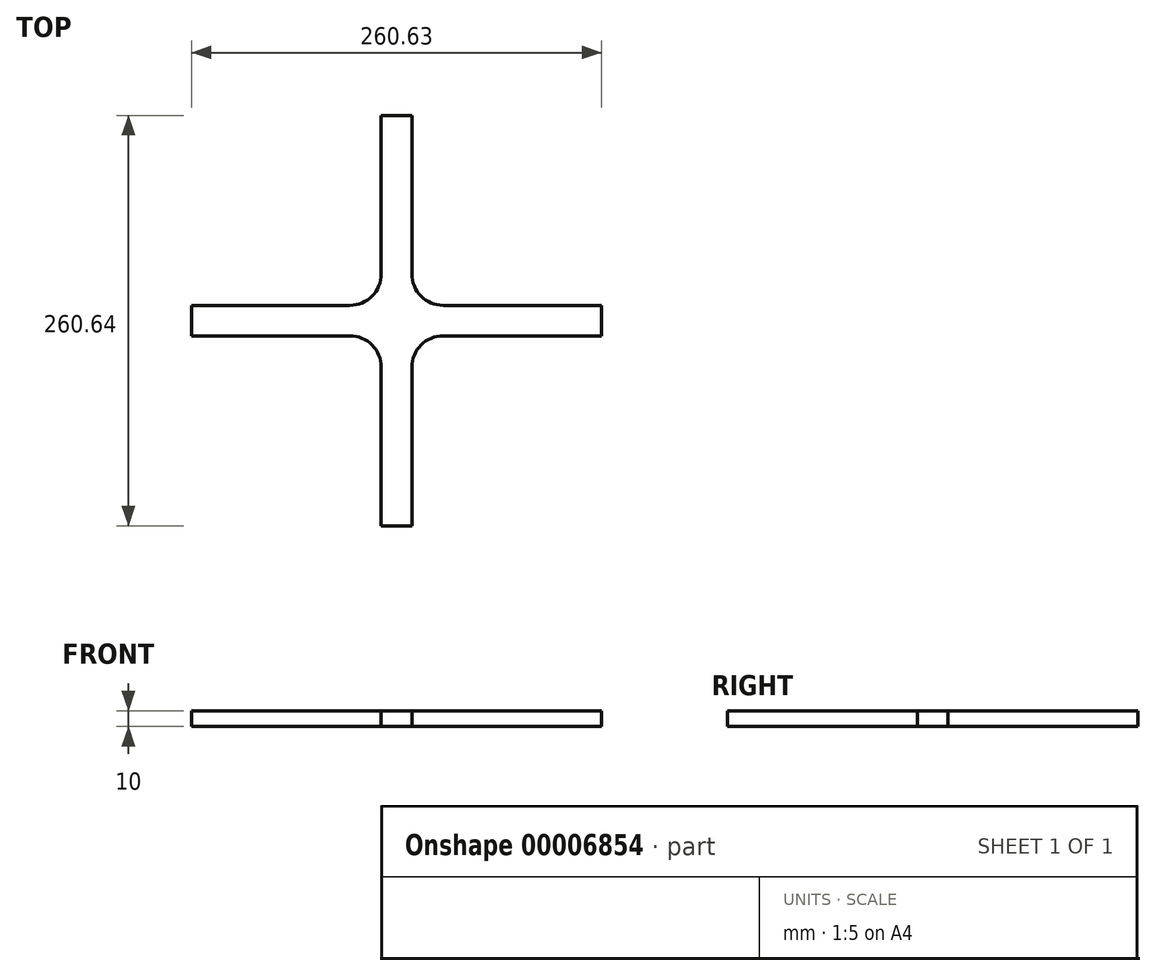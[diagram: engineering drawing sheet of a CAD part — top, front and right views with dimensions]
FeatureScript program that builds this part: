
annotation { "Feature Type Name" : "Feature", "Feature Type Description" : "" }
export const myFeature = defineFeature(function(context is Context, id is Id, definition is map)
    precondition{}
    {
        {
            var Q0;
            Q0=qCreatedBy(makeId("Top.planeOp"),FACE);
            var sketch = newSketch(context, id + "F0", { "sketchPlane" : qUnion([Q0])});
            skLineSegment(sketch, "E0.bottom", {"start": v(21.97, 150.47) * mm, "end": v(41.97, 150.47) * mm});
            skLineSegment(sketch, "E0.top", {"start": v(21.97, -110.77) * mm, "end": v(41.97, -110.77) * mm});
            skLineSegment(sketch, "E0.left", {"start": v(21.97, 150.47) * mm, "end": v(21.97, -110.77) * mm});
            skLineSegment(sketch, "E0.right", {"start": v(41.97, 150.47) * mm, "end": v(41.97, -110.77) * mm});
            skLineSegment(sketch, "E1.bottom", {"start": v(-98.64, 29.85) * mm, "end": v(162.6, 29.85) * mm});
            skLineSegment(sketch, "E1.top", {"start": v(-98.64, 9.85) * mm, "end": v(162.6, 9.85) * mm});
            skLineSegment(sketch, "E1.left", {"start": v(-98.64, 29.85) * mm, "end": v(-98.64, 9.85) * mm});
            skLineSegment(sketch, "E1.right", {"start": v(162.6, 29.85) * mm, "end": v(162.6, 9.85) * mm});
            skPoint(sketch, "E2", {"position": v(31.97, 150.47) * mm});
            skPoint(sketch, "E3", {"position": v(162.6, 19.85) * mm});
            skPoint(sketch, "E4", {"position": v(41.97, 19.85) * mm});
            skPoint(sketch, "E5", {"position": v(31.97, 29.85) * mm});
            skCircle(sketch, "E6", {"center": v(31.97, 19.85) * mm, "radius": 131 * mm});
            skLineSegment(sketch, "E7.0", {"start": v(-98.64, 10.15) * mm, "end": v(162.6, 10.15) * mm});
            skLineSegment(sketch, "E8.0", {"start": v(-98.64, 29.55) * mm, "end": v(162.6, 29.55) * mm});
            skLineSegment(sketch, "E9.0", {"start": v(22.27, 150.47) * mm, "end": v(22.27, -110.77) * mm});
            skLineSegment(sketch, "E10.0", {"start": v(41.67, 150.47) * mm, "end": v(41.67, -110.77) * mm});
            skLineSegment(sketch, "E11.0", {"start": v(-98.34, 29.85) * mm, "end": v(-98.34, 9.85) * mm});
            skLineSegment(sketch, "E12.0", {"start": v(21.97, 150.17) * mm, "end": v(41.97, 150.17) * mm});
            skLineSegment(sketch, "E13.0", {"start": v(162.3, 29.85) * mm, "end": v(162.3, 9.85) * mm});
            skLineSegment(sketch, "E14.0", {"start": v(21.97, -110.47) * mm, "end": v(41.97, -110.47) * mm});
            skSolve(sketch);
        }
        {
            var Q0;
            {var subQ0=sQuery(id+"F0.wireOp",EDGE,"E8.0");var subQ1=sQuery(id+"F0.wireOp",EDGE,"E0.left");var subQ2=makeQuery(id+"F0.imprint","INTERSECT",VERTEX,{"derivedFrom":[subQ1,subQ0]});Q0=makeQuery(id+"F0.imprint","IMPRINT",FACE,{"disambiguationData":[TD([[makeQuery(id+"F0.imprint","IMPRINT",EDGE,{"disambiguationData":[TD([[subQ2,-1.0]])],"derivedFrom":subQ1}),-1.0]])]});}
            var Q1;
            {var subQ0=sQuery(id+"F0.wireOp",EDGE,"E9.0");var subQ1=sQuery(id+"F0.wireOp",EDGE,"E7.0");var subQ2=makeQuery(id+"F0.imprint","INTERSECT",VERTEX,{"derivedFrom":[subQ1,subQ0]});Q1=makeQuery(id+"F0.imprint","IMPRINT",FACE,{"disambiguationData":[TD([[makeQuery(id+"F0.imprint","IMPRINT",EDGE,{"disambiguationData":[TD([[subQ2,-1.0]])],"derivedFrom":subQ1}),1.0]])]});}
            var Q2;
            {var subQ0=sQuery(id+"F0.wireOp",EDGE,"E9.0");var subQ1=sQuery(id+"F0.wireOp",EDGE,"E1.top");var subQ2=makeQuery(id+"F0.imprint","INTERSECT",VERTEX,{"derivedFrom":[subQ1,subQ0]});Q2=makeQuery(id+"F0.imprint","IMPRINT",FACE,{"disambiguationData":[TD([[makeQuery(id+"F0.imprint","IMPRINT",EDGE,{"disambiguationData":[TD([[subQ2,-1.0]])],"derivedFrom":subQ1}),-1.0]])]});}
            var Q3;
            {var subQ0=sQuery(id+"F0.wireOp",EDGE,"E8.0");var subQ1=sQuery(id+"F0.wireOp",EDGE,"E0.right");var subQ2=makeQuery(id+"F0.imprint","INTERSECT",VERTEX,{"derivedFrom":[subQ1,subQ0]});Q3=makeQuery(id+"F0.imprint","IMPRINT",FACE,{"disambiguationData":[TD([[makeQuery(id+"F0.imprint","IMPRINT",EDGE,{"disambiguationData":[TD([[subQ2,-1.0]])],"derivedFrom":subQ1}),1.0]])]});}
            var Q4;
            {var subQ0=sQuery(id+"F0.wireOp",EDGE,"E9.0");var subQ1=sQuery(id+"F0.wireOp",EDGE,"E1.bottom");var subQ2=makeQuery(id+"F0.imprint","INTERSECT",VERTEX,{"derivedFrom":[subQ1,subQ0]});Q4=makeQuery(id+"F0.imprint","IMPRINT",FACE,{"disambiguationData":[TD([[makeQuery(id+"F0.imprint","IMPRINT",EDGE,{"disambiguationData":[TD([[subQ2,-1.0]])],"derivedFrom":subQ1}),1.0]])]});}
            var Q5;
            {var subQ0=sQuery(id+"F0.wireOp",EDGE,"E8.0");var subQ1=sQuery(id+"F0.wireOp",EDGE,"E0.left");var subQ2=makeQuery(id+"F0.imprint","INTERSECT",VERTEX,{"derivedFrom":[subQ1,subQ0]});Q5=makeQuery(id+"F0.imprint","IMPRINT",FACE,{"disambiguationData":[TD([[makeQuery(id+"F0.imprint","IMPRINT",EDGE,{"disambiguationData":[TD([[subQ2,-1.0]])],"derivedFrom":subQ1}),1.0]])]});}
            var Q6;
            {var subQ0=sQuery(id+"F0.wireOp",EDGE,"E9.0");var subQ1=sQuery(id+"F0.wireOp",EDGE,"E1.bottom");var subQ2=makeQuery(id+"F0.imprint","INTERSECT",VERTEX,{"derivedFrom":[subQ1,subQ0]});Q6=makeQuery(id+"F0.imprint","IMPRINT",FACE,{"disambiguationData":[TD([[makeQuery(id+"F0.imprint","IMPRINT",EDGE,{"disambiguationData":[TD([[subQ2,-1.0]])],"derivedFrom":subQ1}),-1.0]])]});}
            var Q7;
            {var subQ0=sQuery(id+"F0.wireOp",EDGE,"E8.0");var subQ1=sQuery(id+"F0.wireOp",EDGE,"E0.right");var subQ2=makeQuery(id+"F0.imprint","INTERSECT",VERTEX,{"derivedFrom":[subQ1,subQ0]});Q7=makeQuery(id+"F0.imprint","IMPRINT",FACE,{"disambiguationData":[TD([[makeQuery(id+"F0.imprint","IMPRINT",EDGE,{"disambiguationData":[TD([[subQ2,-1.0]])],"derivedFrom":subQ1}),-1.0]])]});}
            var Q8;
            {var subQ0=sQuery(id+"F0.wireOp",EDGE,"E9.0");var subQ1=sQuery(id+"F0.wireOp",EDGE,"E1.top");var subQ2=makeQuery(id+"F0.imprint","INTERSECT",VERTEX,{"derivedFrom":[subQ1,subQ0]});Q8=makeQuery(id+"F0.imprint","IMPRINT",FACE,{"disambiguationData":[TD([[makeQuery(id+"F0.imprint","IMPRINT",EDGE,{"disambiguationData":[TD([[subQ2,-1.0]])],"derivedFrom":subQ1}),1.0]])]});}
            extrude(context, id + "F1", {"entities" : qUnion([Q0, Q1, Q2, Q3, Q4, Q5, Q6, Q7, Q8]), "depth" : 10 * mm});
        }
        {
            var Q0;
            Q0=makeQuery(id+"F1.opExtrude","SWEPT_EDGE",EDGE,{"disambiguationData":[OSD([sQuery(id+"F0.wireOp",EDGE,"E8.0"),sQuery(id+"F0.wireOp",EDGE,"E9.0")])]});
            var Q1;
            Q1=makeQuery(id+"F1.opExtrude","SWEPT_EDGE",EDGE,{"disambiguationData":[OSD([sQuery(id+"F0.wireOp",EDGE,"E8.0"),sQuery(id+"F0.wireOp",EDGE,"E10.0")])]});
            var Q2;
            Q2=makeQuery(id+"F1.opExtrude","SWEPT_EDGE",EDGE,{"disambiguationData":[OSD([sQuery(id+"F0.wireOp",EDGE,"E7.0"),sQuery(id+"F0.wireOp",EDGE,"E10.0")])]});
            var Q3;
            Q3=makeQuery(id+"F1.opExtrude","SWEPT_EDGE",EDGE,{"disambiguationData":[OSD([sQuery(id+"F0.wireOp",EDGE,"E7.0"),sQuery(id+"F0.wireOp",EDGE,"E9.0")])]});
            fillet(context, id + "F2", {"entities" : qUnion([Q0, Q1, Q2, Q3]), "radius" : 20 * mm, "tangentPropagation" : true, "allowEdgeOverflow" : false});
        }
    });
